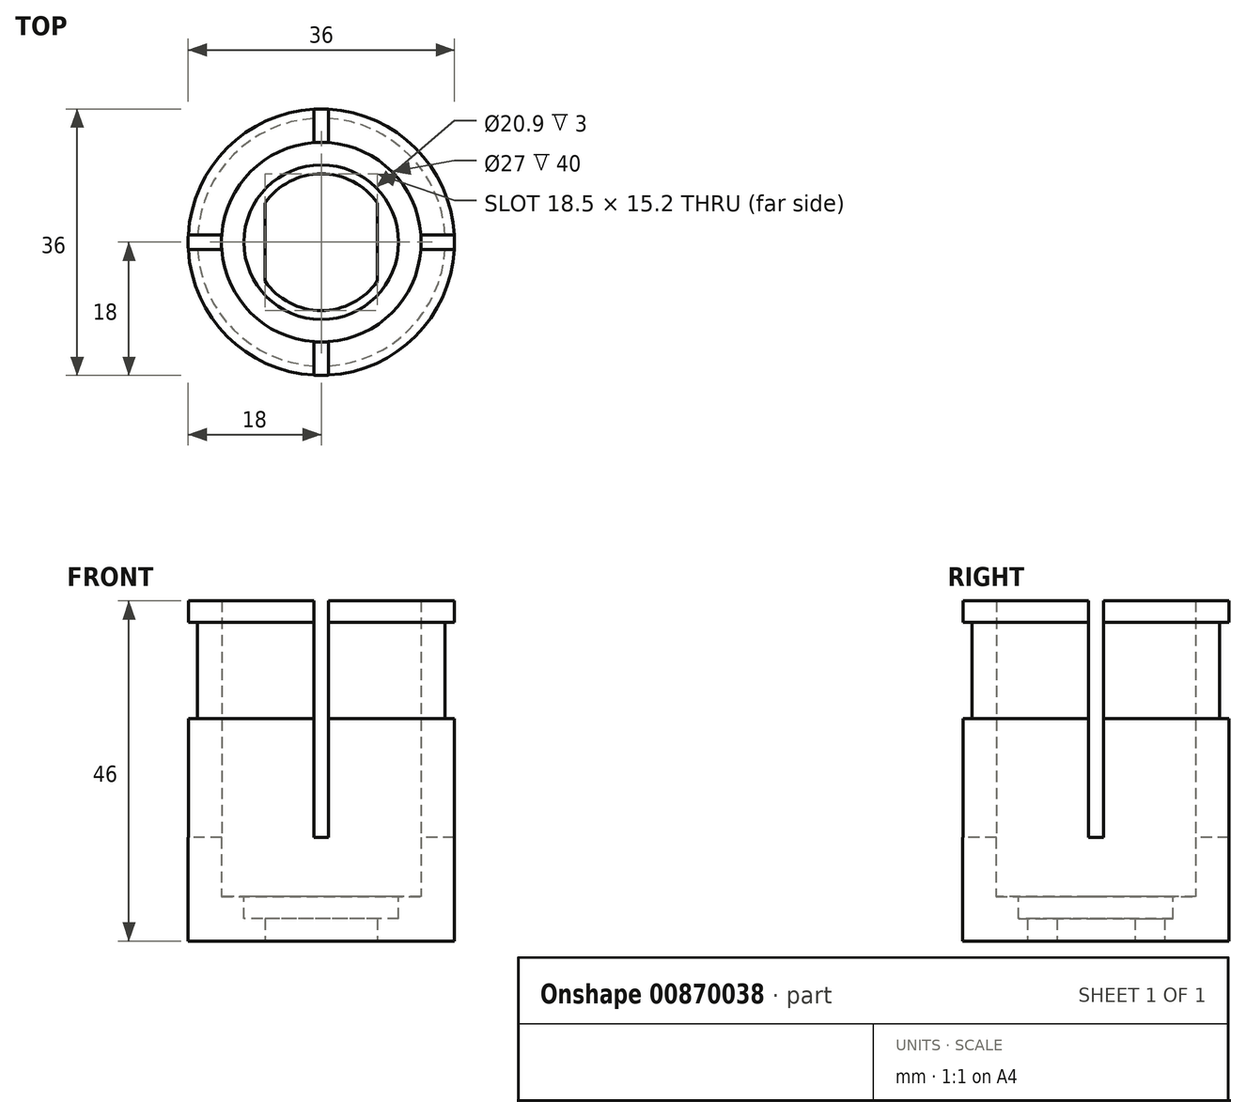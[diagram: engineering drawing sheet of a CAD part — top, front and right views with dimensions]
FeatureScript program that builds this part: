
annotation { "Feature Type Name" : "Feature", "Feature Type Description" : "" }
export const myFeature = defineFeature(function(context is Context, id is Id, definition is map)
    precondition{}
    {
        {
            var Q0;
            Q0=qCreatedBy(makeId("Top.planeOp"),FACE);
            var sketch = newSketch(context, id + "F0", { "sketchPlane" : qUnion([Q0])});
            skCircle(sketch, "E0", {"center": v(0, 0) * mm, "radius": 18 * mm});
            skArc(sketch, "E1", {"start": v(-7.1, -5.11) * mm, "mid": v(0, -8.75) * mm, "end": v(7.1, -5.11) * mm});
            skLineSegment(sketch, "E2", {"start": v(0, 33.14) * mm, "end": v(0, -28.77) * mm, "construction": true});
            skLineSegment(sketch, "E3", {"start": v(7.1, 5.11) * mm, "end": v(7.1, -5.11) * mm});
            skLineSegment(sketch, "E4", {"start": v(-7.1, 5.11) * mm, "end": v(-7.1, -5.11) * mm});
            skArc(sketch, "E5.trimOffspring", {"start": v(7.1, 5.11) * mm, "mid": v(0, 8.75) * mm, "end": v(-7.1, 5.11) * mm});
            skArc(sketch, "E6.0", {"start": v(7.6, 5.27) * mm, "mid": v(0, 9.25) * mm, "end": v(-7.6, 5.27) * mm});
            skLineSegment(sketch, "E6.1", {"start": v(7.6, 5.27) * mm, "end": v(7.6, -5.27) * mm});
            skArc(sketch, "E6.2", {"start": v(-7.6, -5.27) * mm, "mid": v(0, -9.25) * mm, "end": v(7.6, -5.27) * mm});
            skLineSegment(sketch, "E6.3", {"start": v(-7.6, 5.27) * mm, "end": v(-7.6, -5.27) * mm});
            skSolve(sketch);
        }
        {
            var Q0;
            Q0=makeQuery(id+"F0.imprint","IMPRINT",FACE,{"disambiguationData":[TD([[makeQuery(id+"F0.imprint","IMPRINT",EDGE,{"derivedFrom":sQuery(id+"F0.wireOp",EDGE,"E0")}),1.0]])]});
            extrude(context, id + "F1", {"entities" : qUnion([Q0]), "depth" : 10 * mm, "offsetDistance" : 25 * mm});
        }
        {
            var Q0;
            Q0=makeQuery(id+"F1.opExtrude","CAP_FACE",FACE,{"disambiguationData":[OSD([sQuery(id+"F0.wireOp",EDGE,"E0"),sQuery(id+"F0.wireOp",EDGE,"E6.0"),sQuery(id+"F0.wireOp",EDGE,"E6.1"),sQuery(id+"F0.wireOp",EDGE,"E6.2"),sQuery(id+"F0.wireOp",EDGE,"E6.3")])],"isStart":false});
            var sketch = newSketch(context, id + "F2", { "sketchPlane" : qUnion([Q0])});
            skCircle(sketch, "E7", {"center": v(0, 0) * mm, "radius": 10.45 * mm});
            skSolve(sketch);
        }
        {
            var Q0;
            Q0=makeQuery(id+"F2.imprint","IMPRINT",FACE,{"disambiguationData":[TD([[makeQuery(id+"F2.imprint","IMPRINT",EDGE,{"derivedFrom":sQuery(id+"F2.wireOp",EDGE,"E7")}),1.0]])]});
            extrude(context, id + "F3", {"entities" : qUnion([Q0]), "operationType" : NewBodyOperationType.REMOVE, "oppositeDirection" : true, "depth" : 3 * mm, "offsetDistance" : 25 * mm});
        }
        {
            var Q0;
            Q0=makeQuery(id+"F1.opExtrude","CAP_FACE",FACE,{"disambiguationData":[OSD([sQuery(id+"F0.wireOp",EDGE,"E0"),sQuery(id+"F0.wireOp",EDGE,"E6.0"),sQuery(id+"F0.wireOp",EDGE,"E6.1"),sQuery(id+"F0.wireOp",EDGE,"E6.2"),sQuery(id+"F0.wireOp",EDGE,"E6.3")])],"isStart":false});
            var sketch = newSketch(context, id + "F4", { "sketchPlane" : qUnion([Q0])});
            skCircle(sketch, "E8", {"center": v(0, 0) * mm, "radius": 13.5 * mm});
            skSolve(sketch);
        }
        {
            var Q0;
            Q0=makeQuery(id+"F4.imprint","IMPRINT",FACE,{"disambiguationData":[TD([[makeQuery(id+"F4.imprint","IMPRINT",EDGE,{"derivedFrom":sQuery(id+"F4.wireOp",EDGE,"E8")}),-1.0]])]});
            extrude(context, id + "F5", {"entities" : qUnion([Q0]), "operationType" : NewBodyOperationType.ADD, "depth" : 40 * mm, "offsetDistance" : 25 * mm});
        }
        {
            var Q0;
            Q0=qCreatedBy(makeId("Right.planeOp"),FACE);
            var sketch = newSketch(context, id + "F6", { "sketchPlane" : qUnion([Q0])});
            skLineSegment(sketch, "E9.bottom", {"start": v(1, 59.08) * mm, "end": v(-1, 59.08) * mm});
            skLineSegment(sketch, "E9.top", {"start": v(1, 18) * mm, "end": v(-1, 18) * mm});
            skLineSegment(sketch, "E9.left", {"start": v(1, 59.08) * mm, "end": v(1, 18) * mm});
            skLineSegment(sketch, "E9.right", {"start": v(-1, 59.08) * mm, "end": v(-1, 18) * mm});
            skPoint(sketch, "E9.middle", {"position": v(0, 38.54) * mm});
            skSolve(sketch);
        }
        {
            var Q0;
            Q0=makeQuery(id+"F6.imprint","IMPRINT",FACE,{"disambiguationData":[TD([[makeQuery(id+"F6.imprint","IMPRINT",EDGE,{"derivedFrom":sQuery(id+"F6.wireOp",EDGE,"E9.bottom")}),1.0]])]});
            extrude(context, id + "F7", {"entities" : qUnion([Q0]), "operationType" : NewBodyOperationType.REMOVE, "endBound" : BoundingType.SYMMETRIC, "depth" : 40 * mm, "offsetDistance" : 25 * mm});
        }
        {
            var Q0;
            Q0=qCreatedBy(makeId("Front.planeOp"),FACE);
            var sketch = newSketch(context, id + "F8", { "sketchPlane" : qUnion([Q0])});
            skLineSegment(sketch, "E10.bottom", {"start": v(-1, 61.18) * mm, "end": v(1, 61.18) * mm});
            skLineSegment(sketch, "E10.top", {"start": v(-1, 18) * mm, "end": v(1, 18) * mm});
            skLineSegment(sketch, "E10.left", {"start": v(-1, 61.18) * mm, "end": v(-1, 18) * mm});
            skLineSegment(sketch, "E10.right", {"start": v(1, 61.18) * mm, "end": v(1, 18) * mm});
            skPoint(sketch, "E10.middle", {"position": v(0, 39.59) * mm});
            skSolve(sketch);
        }
        {
            var Q0;
            Q0 = qSketchRegion(id + "F8", true);
            extrude(context, id + "F9", {"entities" : qUnion([Q0]), "operationType" : NewBodyOperationType.REMOVE, "endBound" : BoundingType.SYMMETRIC, "oppositeDirection" : true, "depth" : 40 * mm, "offsetDistance" : 25 * mm});
        }
        {
            var Q0;
            Q0=qCreatedBy(makeId("Right.planeOp"),FACE);
            var sketch = newSketch(context, id + "F10", { "sketchPlane" : qUnion([Q0])});
            skLineSegment(sketch, "E11.bottom", {"start": v(16.75, 34.06) * mm, "end": v(18.25, 34.06) * mm});
            skLineSegment(sketch, "E11.top", {"start": v(16.75, 47.06) * mm, "end": v(18.25, 47.06) * mm});
            skLineSegment(sketch, "E11.left", {"start": v(16.75, 34.06) * mm, "end": v(16.75, 47.06) * mm});
            skLineSegment(sketch, "E11.right", {"start": v(18.25, 34.06) * mm, "end": v(18.25, 47.06) * mm});
            skPoint(sketch, "E11.middle", {"position": v(17.5, 40.56) * mm});
            skSolve(sketch);
        }
        {
            var Q0;
            Q0 = qSketchRegion(id + "F10", true);
            var Q1;
            Q1=makeQuery(id+"F5.opExtrude","SWEPT_FACE",FACE,{"disambiguationData":[OSD([sQuery(id+"F4.wireOp",EDGE,"E8")])]});
            revolve(context, id + "F11", {"operationType" : NewBodyOperationType.REMOVE, "surfaceOperationType" : NewSurfaceOperationType.NEW, "entities" : qUnion([Q0]), "axis" : qUnion([Q1]), "revolveType" : RevolveType.FULL, "oppositeDirection" : true});
        }
        {
            var Q0;
            Q0=makeQuery(id+"F1.opExtrude","CAP_FACE",FACE,{"disambiguationData":[OSD([sQuery(id+"F0.wireOp",EDGE,"E0"),sQuery(id+"F0.wireOp",EDGE,"E6.0"),sQuery(id+"F0.wireOp",EDGE,"E6.1"),sQuery(id+"F0.wireOp",EDGE,"E6.2"),sQuery(id+"F0.wireOp",EDGE,"E6.3")])],"isStart":true});
            extrude(context, id + "F12", {"entities" : qUnion([Q0]), "operationType" : NewBodyOperationType.ADD, "oppositeDirection" : true, "depth" : 3.2 * mm, "offsetDistance" : 25 * mm});
        }
        {
            var Q0;
            Q0=makeQuery(id+"F1.opExtrude","CAP_FACE",FACE,{"disambiguationData":[OSD([sQuery(id+"F0.wireOp",EDGE,"E0"),sQuery(id+"F0.wireOp",EDGE,"E6.0"),sQuery(id+"F0.wireOp",EDGE,"E6.1"),sQuery(id+"F0.wireOp",EDGE,"E6.2"),sQuery(id+"F0.wireOp",EDGE,"E6.3")])],"isStart":true});
            extrude(context, id + "F13", {"entities" : qUnion([Q0]), "operationType" : NewBodyOperationType.REMOVE, "oppositeDirection" : true, "depth" : 4 * mm, "offsetDistance" : 25 * mm});
        }
    });
